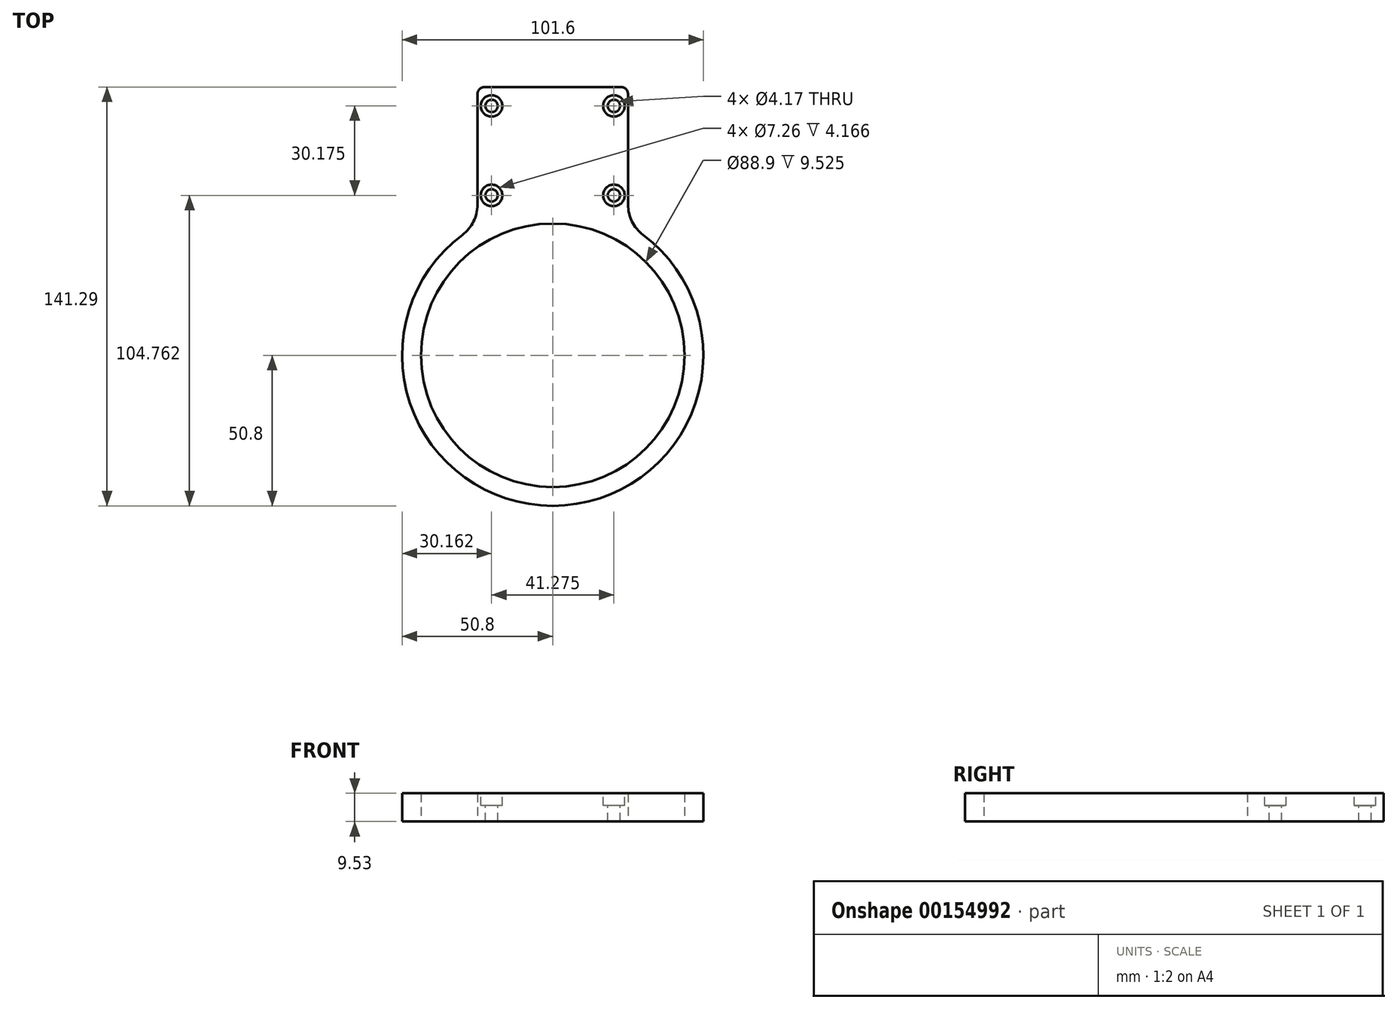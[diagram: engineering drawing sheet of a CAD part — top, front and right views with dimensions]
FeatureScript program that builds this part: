
annotation { "Feature Type Name" : "Feature", "Feature Type Description" : "" }
export const myFeature = defineFeature(function(context is Context, id is Id, definition is map)
    precondition{}
    {
        {
            var Q0;
            Q0=qCreatedBy(makeId("Top.planeOp"),FACE);
            var sketch = newSketch(context, id + "F0", { "sketchPlane" : qUnion([Q0])});
            skCircle(sketch, "E0", {"center": v(0, 0) * mm, "radius": 44.45 * mm});
            skArc(sketch, "E1", {"start": v(-25.4, 44) * mm, "mid": v(0, -50.8) * mm, "end": v(25.4, 44) * mm});
            skLineSegment(sketch, "E2", {"start": v(-25.4, 44) * mm, "end": v(-25.4, 90.49) * mm});
            skLineSegment(sketch, "E3", {"start": v(-25.4, 90.49) * mm, "end": v(25.4, 90.49) * mm});
            skLineSegment(sketch, "E4", {"start": v(25.4, 90.49) * mm, "end": v(25.4, 44) * mm});
            skLineSegment(sketch, "E5", {"start": v(0, 143.03) * mm, "end": v(0, 0) * mm, "construction": true});
            skSolve(sketch);
        }
        {
            var Q0;
            Q0=makeQuery(id+"F0.imprint","IMPRINT",FACE,{"disambiguationData":[TD([[makeQuery(id+"F0.imprint","IMPRINT",EDGE,{"derivedFrom":sQuery(id+"F0.wireOp",EDGE,"E0")}),-1.0]])]});
            extrude(context, id + "F1", {"entities" : qUnion([Q0]), "depth" : 9.52 * mm});
        }
        {
            var Q0;
            Q0=makeQuery(id+"F1.opExtrude","CAP_FACE",FACE,{"disambiguationData":[OSD([sQuery(id+"F0.wireOp",EDGE,"E0"),sQuery(id+"F0.wireOp",EDGE,"E1"),sQuery(id+"F0.wireOp",EDGE,"E2"),sQuery(id+"F0.wireOp",EDGE,"E3"),sQuery(id+"F0.wireOp",EDGE,"E4")])],"isStart":false});
            var sketch = newSketch(context, id + "F2", { "sketchPlane" : qUnion([Q0])});
            skLineSegment(sketch, "E6.bottom", {"start": v(-20.64, 84.14) * mm, "end": v(20.64, 84.14) * mm, "construction": true});
            skLineSegment(sketch, "E6.top", {"start": v(-20.64, 53.96) * mm, "end": v(20.64, 53.96) * mm, "construction": true});
            skLineSegment(sketch, "E6.left", {"start": v(-20.64, 84.14) * mm, "end": v(-20.64, 53.96) * mm, "construction": true});
            skLineSegment(sketch, "E6.right", {"start": v(20.64, 84.14) * mm, "end": v(20.64, 53.96) * mm, "construction": true});
            skCircle(sketch, "E7", {"center": v(-20.64, 84.14) * mm, "radius": 2.08 * mm});
            skCircle(sketch, "E8", {"center": v(20.64, 84.14) * mm, "radius": 2.08 * mm});
            skCircle(sketch, "E9", {"center": v(20.64, 53.96) * mm, "radius": 2.08 * mm});
            skCircle(sketch, "E10", {"center": v(-20.64, 53.96) * mm, "radius": 2.08 * mm});
            skSolve(sketch);
        }
        {
            var Q0;
            Q0 = qSketchRegion(id + "F2", true);
            extrude(context, id + "F3", {"entities" : qUnion([Q0]), "operationType" : NewBodyOperationType.REMOVE, "oppositeDirection" : true, "depth" : 25.4 * mm});
        }
        {
            var Q0;
            Q0=makeQuery(id+"F1.opExtrude","CAP_FACE",FACE,{"disambiguationData":[OSD([sQuery(id+"F0.wireOp",EDGE,"E0"),sQuery(id+"F0.wireOp",EDGE,"E1"),sQuery(id+"F0.wireOp",EDGE,"E2"),sQuery(id+"F0.wireOp",EDGE,"E3"),sQuery(id+"F0.wireOp",EDGE,"E4")])],"isStart":false});
            var sketch = newSketch(context, id + "F4", { "sketchPlane" : qUnion([Q0])});
            skCircle(sketch, "E11", {"center": v(-20.64, 84.14) * mm, "radius": 3.63 * mm});
            skCircle(sketch, "E12", {"center": v(20.64, 84.14) * mm, "radius": 3.63 * mm});
            skCircle(sketch, "E13", {"center": v(20.64, 53.96) * mm, "radius": 3.63 * mm});
            skCircle(sketch, "E14", {"center": v(-20.64, 53.96) * mm, "radius": 3.63 * mm});
            skSolve(sketch);
        }
        {
            var Q0;
            Q0 = qSketchRegion(id + "F4", true);
            extrude(context, id + "F5", {"entities" : qUnion([Q0]), "operationType" : NewBodyOperationType.REMOVE, "oppositeDirection" : true, "depth" : 4.17 * mm});
        }
        {
            var Q0;
            Q0=makeQuery(id+"F1.opExtrude","SWEPT_EDGE",EDGE,{"disambiguationData":[OSD([sQuery(id+"F0.wireOp",EDGE,"E2"),sQuery(id+"F0.wireOp",EDGE,"E3")])]});
            var Q1;
            Q1=makeQuery(id+"F1.opExtrude","SWEPT_EDGE",EDGE,{"disambiguationData":[OSD([sQuery(id+"F0.wireOp",EDGE,"E3"),sQuery(id+"F0.wireOp",EDGE,"E4")])]});
            fillet(context, id + "F6", {"entities" : qUnion([Q0, Q1]), "radius" : 2.38 * mm, "tangentPropagation" : true, "allowEdgeOverflow" : false});
        }
        {
            var Q0;
            Q0=makeQuery(id+"F1.opExtrude","SWEPT_EDGE",EDGE,{"disambiguationData":[OSD([sQuery(id+"F0.wireOp",EDGE,"E1"),sQuery(id+"F0.wireOp",EDGE,"E2")])]});
            var Q1;
            Q1=makeQuery(id+"F1.opExtrude","SWEPT_EDGE",EDGE,{"disambiguationData":[OSD([sQuery(id+"F0.wireOp",EDGE,"E1"),sQuery(id+"F0.wireOp",EDGE,"E4")])]});
            fillet(context, id + "F7", {"entities" : qUnion([Q0, Q1]), "radius" : 12.7 * mm, "tangentPropagation" : true, "allowEdgeOverflow" : false});
        }
    });
